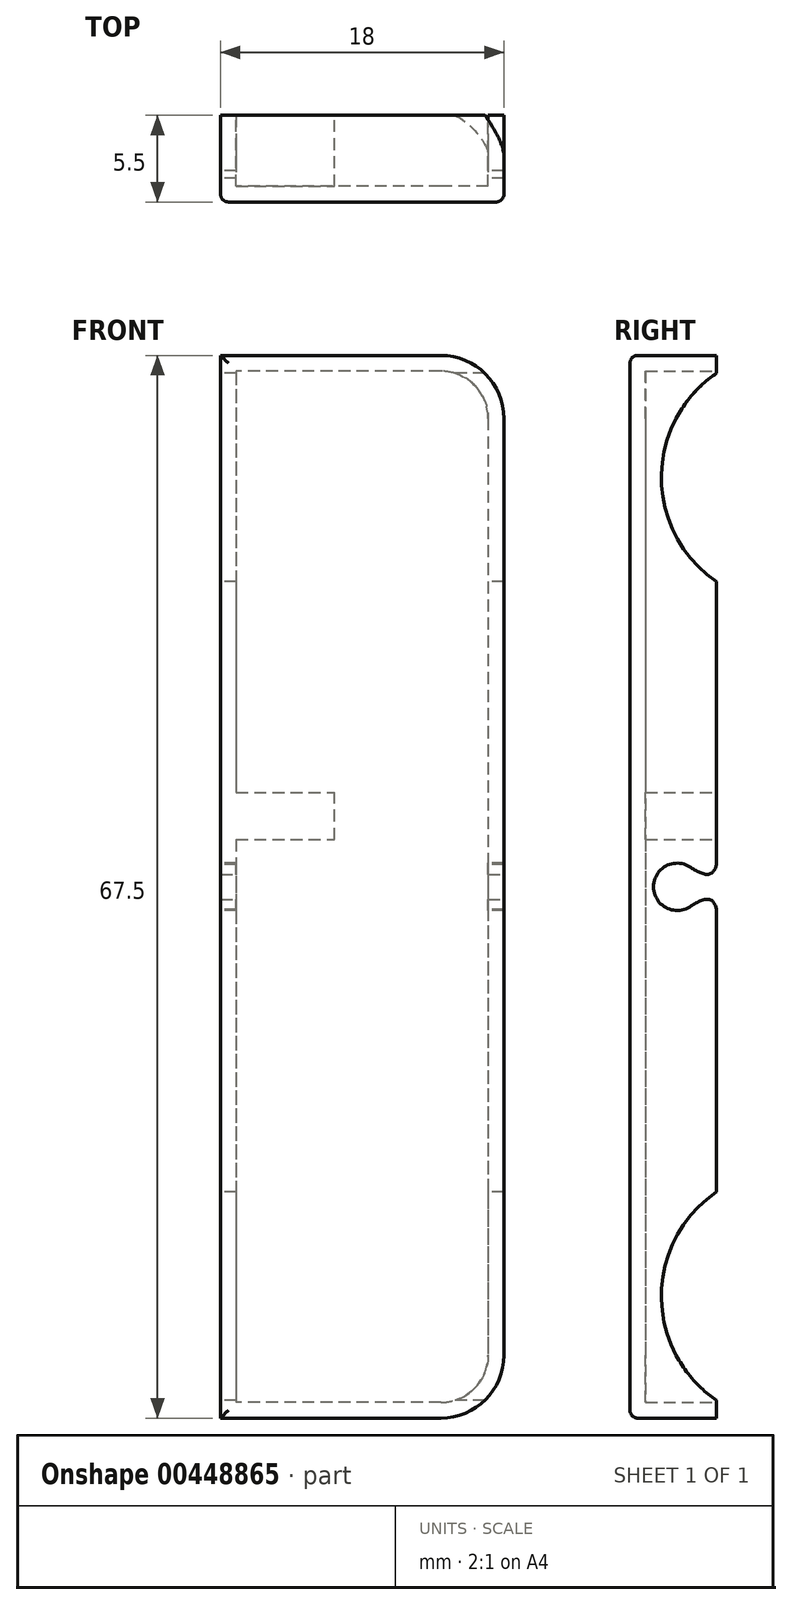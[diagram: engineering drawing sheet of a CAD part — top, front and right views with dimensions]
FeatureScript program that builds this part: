
annotation { "Feature Type Name" : "Feature", "Feature Type Description" : "" }
export const myFeature = defineFeature(function(context is Context, id is Id, definition is map)
    precondition{}
    {
        {
            var Q0;
            Q0=qCreatedBy(makeId("Front.planeOp"),FACE);
            var sketch = newSketch(context, id + "F0", { "sketchPlane" : qUnion([Q0])});
            skLineSegment(sketch, "E0.0", {"start": v(19.75, 29.75) * mm, "end": v(19.75, -29.75) * mm});
            skLineSegment(sketch, "E0.1", {"start": v(15.75, 33.75) * mm, "end": v(1.75, 33.75) * mm});
            skLineSegment(sketch, "E0.3", {"start": v(15.75, -33.75) * mm, "end": v(1.75, -33.75) * mm});
            skPoint(sketch, "E1.visualSharp", {"position": v(19.75, 33.75) * mm});
            skArc(sketch, "E1.filletArc", {"start": v(19.75, 29.75) * mm, "mid": v(18.58, 32.58) * mm, "end": v(15.75, 33.75) * mm});
            skPoint(sketch, "E2.visualSharp", {"position": v(19.75, -33.75) * mm});
            skArc(sketch, "E2.filletArc", {"start": v(15.75, -33.75) * mm, "mid": v(18.58, -32.58) * mm, "end": v(19.75, -29.75) * mm});
            skLineSegment(sketch, "E3", {"start": v(1.75, 33.75) * mm, "end": v(1.75, -33.75) * mm});
            skSolve(sketch);
        }
        {
            var Q0;
            Q0 = qSketchRegion(id + "F0", true);
            extrude(context, id + "F1", {"entities" : qUnion([Q0]), "depth" : 16 * mm, "hasSecondDirection" : true, "secondDirectionOppositeDirection" : false, "secondDirectionDepth" : 10.5 * mm});
        }
        {
            var Q0;
            Q0=qCreatedBy(makeId("Right.planeOp"),FACE);
            var sketch = newSketch(context, id + "F2", { "sketchPlane" : qUnion([Q0])});
            skCircle(sketch, "E4", {"center": v(-13, 0) * mm, "radius": 1.5 * mm});
            skCircle(sketch, "E5", {"center": v(-6, -26) * mm, "radius": 8 * mm});
            skFitSpline(sketch, "E6", {"points": [v(-10.5, 1.43) * mm, v(-12.2, 1.27) * mm], "startDerivative": vector(-0.68, -3.3) * mm, "endDerivative": vector(-1.64, 1.04) * mm});
            skFitSpline(sketch, "E7.MirrorCS", {"points": [v(-10.5, -1.43) * mm, v(-12.2, -1.27) * mm], "startDerivative": vector(-0.68, 3.3) * mm, "endDerivative": vector(-1.64, -1.04) * mm});
            skLineSegment(sketch, "E8.bottom", {"start": v(-10.5, 1.43) * mm, "end": v(-9.98, 1.43) * mm});
            skLineSegment(sketch, "E8.top", {"start": v(-10.5, -1.43) * mm, "end": v(-9.98, -1.43) * mm});
            skLineSegment(sketch, "E8.left", {"start": v(-10.5, 1.43) * mm, "end": v(-10.5, -1.43) * mm});
            skLineSegment(sketch, "E8.right", {"start": v(-9.98, 1.43) * mm, "end": v(-9.98, -1.43) * mm});
            skPoint(sketch, "E8.middle", {"position": v(-10.24, 0) * mm});
            skPoint(sketch, "E9", {"position": v(-10.5, 0) * mm});
            skCircle(sketch, "E10.MirrorC", {"center": v(-6, 26) * mm, "radius": 8 * mm});
            skSolve(sketch);
        }
        {
            var Q0;
            Q0=makeQuery(id+"F1.opExtrude","CAP_FACE",FACE,{"disambiguationData":[OSD([sQuery(id+"F0.wireOp",EDGE,"E0.0"),sQuery(id+"F0.wireOp",EDGE,"E0.1"),sQuery(id+"F0.wireOp",EDGE,"E0.3"),sQuery(id+"F0.wireOp",EDGE,"E1.filletArc"),sQuery(id+"F0.wireOp",EDGE,"E2.filletArc"),sQuery(id+"F0.wireOp",EDGE,"E3")])],"isStart":true});
            shell(context, id + "F3", {"entities" : qUnion([Q0]), "thickness" : 1 * mm});
        }
        {
            var Q0;
            Q0 = qSketchRegion(id + "F2", true);
            extrude(context, id + "F4", {"entities" : qUnion([Q0]), "operationType" : NewBodyOperationType.REMOVE, "endBound" : BoundingType.THROUGH_ALL, "depth" : 25 * mm});
        }
        {
            var Q0;
            Q0=makeQuery(id+"F1.opExtrude","CAP_FACE",FACE,{"disambiguationData":[OSD([sQuery(id+"F0.wireOp",EDGE,"E0.0"),sQuery(id+"F0.wireOp",EDGE,"E0.1"),sQuery(id+"F0.wireOp",EDGE,"E0.3"),sQuery(id+"F0.wireOp",EDGE,"E1.filletArc"),sQuery(id+"F0.wireOp",EDGE,"E2.filletArc"),sQuery(id+"F0.wireOp",EDGE,"E3")])],"isStart":false});
            fillet(context, id + "F5", {"entities" : qUnion([Q0]), "radius" : 0.5 * mm, "tangentPropagation" : true, "allowEdgeOverflow" : false});
        }
        {
            var Q0;
            {var subQ0=sQuery(id+"F0.wireOp",EDGE,"E3");var subQ1=sQuery(id+"F0.wireOp",EDGE,"E0.1");var subQ2=sQuery(id+"F0.wireOp",EDGE,"E1.filletArc");var subQ3=sQuery(id+"F0.wireOp",EDGE,"E0.0");Q0=makeQuery(id+"F4.boolean.opBoolean","SPLIT",FACE,{"disambiguationData":[TD([makeQuery(id+"F1.opExtrude","SWEPT_FACE",FACE,{"disambiguationData":[OSD([subQ3])]}),makeQuery(id+"F1.opExtrude","SWEPT_FACE",FACE,{"disambiguationData":[OSD([subQ1])]}),makeQuery(id+"F1.opExtrude","SWEPT_FACE",FACE,{"disambiguationData":[OSD([subQ2])]}),makeQuery(id+"F1.opExtrude","SWEPT_FACE",FACE,{"disambiguationData":[OSD([subQ0])]}),makeQuery(id+"F3.opShell","OFFSET_FACE",FACE,{"disambiguationData":[OSD([subQ3])]}),makeQuery(id+"F3.opShell","OFFSET_FACE",FACE,{"disambiguationData":[OSD([subQ1])]}),makeQuery(id+"F3.opShell","OFFSET_FACE",FACE,{"disambiguationData":[OSD([subQ2])]}),makeQuery(id+"F3.opShell","OFFSET_FACE",FACE,{"disambiguationData":[OSD([subQ0])]}),makeQuery(id+"F4.opExtrude","SWEPT_FACE",FACE,{"disambiguationData":[OSD([sQuery(id+"F2.wireOp",EDGE,"E8.bottom")])]})])],"derivedFrom":makeQuery(id+"F1.opExtrude","CAP_FACE",FACE,{"disambiguationData":[OSD([subQ3,subQ1,sQuery(id+"F0.wireOp",EDGE,"E0.3"),subQ2,sQuery(id+"F0.wireOp",EDGE,"E2.filletArc"),subQ0])],"isStart":true})});}
            var sketch = newSketch(context, id + "F6", { "sketchPlane" : qUnion([Q0])});
            skLineSegment(sketch, "E11.bottom", {"start": v(-2.75, 3) * mm, "end": v(-9, 3) * mm});
            skLineSegment(sketch, "E11.top", {"start": v(-2.75, 6) * mm, "end": v(-9, 6) * mm});
            skLineSegment(sketch, "E11.left", {"start": v(-2.75, 3) * mm, "end": v(-2.75, 6) * mm});
            skLineSegment(sketch, "E11.right", {"start": v(-9, 3) * mm, "end": v(-9, 6) * mm});
            skSolve(sketch);
        }
        {
            var Q0;
            Q0 = qSketchRegion(id + "F6", true);
            var Q1;
            Q1=makeQuery(id+"F3.opShell","OFFSET_FACE",FACE,{"disambiguationData":[OSD([sQuery(id+"F0.wireOp",EDGE,"E0.0"),sQuery(id+"F0.wireOp",EDGE,"E0.1"),sQuery(id+"F0.wireOp",EDGE,"E0.3"),sQuery(id+"F0.wireOp",EDGE,"E1.filletArc"),sQuery(id+"F0.wireOp",EDGE,"E2.filletArc"),sQuery(id+"F0.wireOp",EDGE,"E3")])]});
            extrude(context, id + "F7", {"entities" : qUnion([Q0]), "operationType" : NewBodyOperationType.ADD, "endBound" : BoundingType.UP_TO_SURFACE, "oppositeDirection" : true, "endBoundEntityFace" : qUnion([Q1]), "depth" : 25 * mm});
        }
    });
